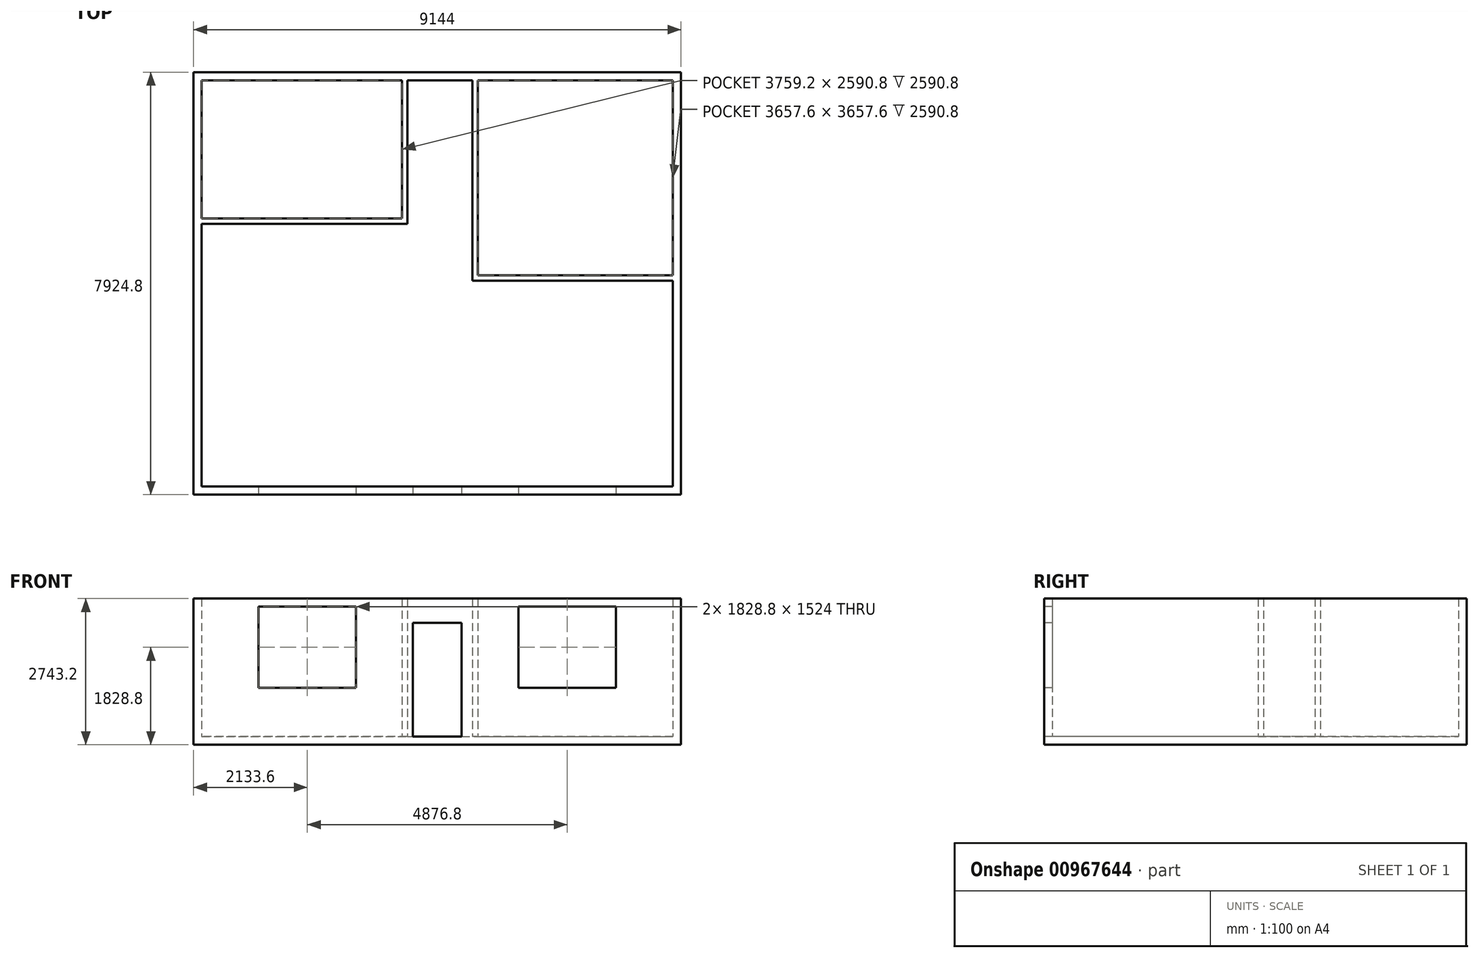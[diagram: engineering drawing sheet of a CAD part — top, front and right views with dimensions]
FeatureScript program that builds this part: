
annotation { "Feature Type Name" : "Feature", "Feature Type Description" : "" }
export const myFeature = defineFeature(function(context is Context, id is Id, definition is map)
    precondition{}
    {
        {
            var Q0;
            Q0=qCreatedBy(makeId("Top.planeOp"),FACE);
            var sketch = newSketch(context, id + "F0", { "sketchPlane" : qUnion([Q0])});
            skLineSegment(sketch, "E0.bottom", {"start": v(-4572, 3962.4) * mm, "end": v(4572, 3962.4) * mm});
            skLineSegment(sketch, "E0.top", {"start": v(-4572, -3962.4) * mm, "end": v(4572, -3962.4) * mm});
            skLineSegment(sketch, "E0.left", {"start": v(-4572, 3962.4) * mm, "end": v(-4572, -3962.4) * mm});
            skLineSegment(sketch, "E0.right", {"start": v(4572, 3962.4) * mm, "end": v(4572, -3962.4) * mm});
            skPoint(sketch, "E0.middle", {"position": v(0, 0) * mm});
            skSolve(sketch);
        }
        {
            var Q0;
            Q0=makeQuery(id+"F0.imprint","IMPRINT",FACE,{"disambiguationData":[TD([[makeQuery(id+"F0.imprint","IMPRINT",EDGE,{"derivedFrom":sQuery(id+"F0.wireOp",EDGE,"E0.bottom")}),-1.0]])]});
            extrude(context, id + "F1", {"entities" : qUnion([Q0]), "flatOperationType" : FlatOperationType.REMOVE, "depth" : 2743.2 * mm, "offsetDistance" : 30.48 * mm, "domain" : OperationDomain.MODEL});
        }
        {
            var Q0;
            Q0=makeQuery(id+"F1.opExtrude","CAP_FACE",FACE,{"disambiguationData":[OSD([sQuery(id+"F0.wireOp",EDGE,"E0.bottom"),sQuery(id+"F0.wireOp",EDGE,"E0.top"),sQuery(id+"F0.wireOp",EDGE,"E0.left"),sQuery(id+"F0.wireOp",EDGE,"E0.right")])],"isStart":false});
            shell(context, id + "F2", {"entities" : qUnion([Q0]), "thickness" : 152.4 * mm});
        }
        {
            var Q0;
            Q0=makeQuery(id+"F1.opExtrude","SWEPT_FACE",FACE,{"disambiguationData":[OSD([sQuery(id+"F0.wireOp",EDGE,"E0.top")])]});
            var sketch = newSketch(context, id + "F3", { "sketchPlane" : qUnion([Q0])});
            skLineSegment(sketch, "E1.bottom", {"start": v(457.2, 2286) * mm, "end": v(-457.2, 2286) * mm});
            skLineSegment(sketch, "E1.top", {"start": v(457.2, 152.4) * mm, "end": v(-457.2, 152.4) * mm});
            skLineSegment(sketch, "E1.left", {"start": v(457.2, 2286) * mm, "end": v(457.2, 152.4) * mm});
            skLineSegment(sketch, "E1.right", {"start": v(-457.2, 2286) * mm, "end": v(-457.2, 152.4) * mm});
            skPoint(sketch, "E1.middle", {"position": v(0, 1219.2) * mm});
            skLineSegment(sketch, "E2.bottom", {"start": v(-3352.8, 3657.6) * mm, "end": v(-914.4, 3657.6) * mm});
            skLineSegment(sketch, "E2.top", {"start": v(-3352.8, 6096) * mm, "end": v(-914.4, 6096) * mm});
            skLineSegment(sketch, "E2.left", {"start": v(-3352.8, 3657.6) * mm, "end": v(-3352.8, 6096) * mm});
            skLineSegment(sketch, "E2.right", {"start": v(-914.4, 3657.6) * mm, "end": v(-914.4, 6096) * mm});
            skPoint(sketch, "E2.middle", {"position": v(-2133.6, 4876.8) * mm});
            skLineSegment(sketch, "E3.bottom", {"start": v(914.4, 3657.6) * mm, "end": v(3352.8, 3657.6) * mm});
            skLineSegment(sketch, "E3.top", {"start": v(914.4, 6096) * mm, "end": v(3352.8, 6096) * mm});
            skLineSegment(sketch, "E3.left", {"start": v(914.4, 3657.6) * mm, "end": v(914.4, 6096) * mm});
            skLineSegment(sketch, "E3.right", {"start": v(3352.8, 3657.6) * mm, "end": v(3352.8, 6096) * mm});
            skPoint(sketch, "E3.middle", {"position": v(2133.6, 4876.8) * mm});
            skLineSegment(sketch, "E4.bottom", {"start": v(-3352.8, 2590.8) * mm, "end": v(-1524, 2590.8) * mm});
            skLineSegment(sketch, "E4.top", {"start": v(-3352.8, 1066.8) * mm, "end": v(-1524, 1066.8) * mm});
            skLineSegment(sketch, "E4.left", {"start": v(-3352.8, 2590.8) * mm, "end": v(-3352.8, 1066.8) * mm});
            skLineSegment(sketch, "E4.right", {"start": v(-1524, 2590.8) * mm, "end": v(-1524, 1066.8) * mm});
            skPoint(sketch, "E4.middle", {"position": v(-2438.4, 1828.8) * mm});
            skLineSegment(sketch, "E5.bottom", {"start": v(1524, 2590.8) * mm, "end": v(3352.8, 2590.8) * mm});
            skLineSegment(sketch, "E5.top", {"start": v(1524, 1066.8) * mm, "end": v(3352.8, 1066.8) * mm});
            skLineSegment(sketch, "E5.left", {"start": v(1524, 2590.8) * mm, "end": v(1524, 1066.8) * mm});
            skLineSegment(sketch, "E5.right", {"start": v(3352.8, 2590.8) * mm, "end": v(3352.8, 1066.8) * mm});
            skPoint(sketch, "E5.middle", {"position": v(2438.4, 1828.8) * mm});
            skLineSegment(sketch, "E6", {"start": v(-3352.8, 1066.8) * mm, "end": v(-4572, 1066.8) * mm, "construction": true});
            skLineSegment(sketch, "E7", {"start": v(3352.8, 1066.8) * mm, "end": v(4572, 1066.8) * mm, "construction": true});
            skSolve(sketch);
        }
        {
            var Q0;
            Q0 = qSketchRegion(id + "F3", true);
            var Q1;
            Q1=makeQuery(id+"F2.opShell","OFFSET_FACE",FACE,{"disambiguationData":[OSD([sQuery(id+"F0.wireOp",EDGE,"E0.top")])]});
            extrude(context, id + "F4", {"entities" : qUnion([Q0]), "operationType" : NewBodyOperationType.REMOVE, "endBound" : BoundingType.UP_TO_SURFACE, "oppositeDirection" : true, "depth" : 30.48 * mm, "endBoundEntityFace" : qUnion([Q1]), "offsetDistance" : 30.48 * mm});
        }
        {
            var Q0;
            Q0=makeQuery(id+"F4.boolean.opBoolean","MERGE",FACE,{"derivedFrom":[makeQuery(id+"F2.opShell","OFFSET_FACE",FACE,{"disambiguationData":[OSD([sQuery(id+"F0.wireOp",EDGE,"E0.bottom"),sQuery(id+"F0.wireOp",EDGE,"E0.top"),sQuery(id+"F0.wireOp",EDGE,"E0.left"),sQuery(id+"F0.wireOp",EDGE,"E0.right")])]})],"fromTools":[makeQuery(id+"F4.opExtrude","SWEPT_FACE",FACE,{"disambiguationData":[OSD([sQuery(id+"F3.wireOp",EDGE,"E1.top")])]})]});
            var sketch = newSketch(context, id + "F5", { "sketchPlane" : qUnion([Q0])});
            skLineSegment(sketch, "E8", {"start": v(4419.6, 50.8) * mm, "end": v(660.4, 50.8) * mm});
            skLineSegment(sketch, "E9", {"start": v(660.4, 50.8) * mm, "end": v(660.4, 3810) * mm});
            skLineSegment(sketch, "E10", {"start": v(660.4, 3810) * mm, "end": v(762, 3810) * mm});
            skLineSegment(sketch, "E11", {"start": v(762, 3810) * mm, "end": v(762, 152.4) * mm});
            skLineSegment(sketch, "E12", {"start": v(762, 152.4) * mm, "end": v(4419.6, 152.4) * mm});
            skLineSegment(sketch, "E13", {"start": v(4419.6, 152.4) * mm, "end": v(4419.6, 50.8) * mm});
            skLineSegment(sketch, "E14", {"start": v(-558.8, 3810) * mm, "end": v(-558.8, 1117.6) * mm});
            skLineSegment(sketch, "E15", {"start": v(-558.8, 1117.6) * mm, "end": v(-4419.6, 1117.6) * mm});
            skLineSegment(sketch, "E16", {"start": v(-4419.6, 1117.6) * mm, "end": v(-4419.6, 1219.2) * mm});
            skLineSegment(sketch, "E17", {"start": v(-4419.6, 1219.2) * mm, "end": v(-660.4, 1219.2) * mm});
            skLineSegment(sketch, "E18", {"start": v(-660.4, 1219.2) * mm, "end": v(-660.4, 3810) * mm});
            skLineSegment(sketch, "E19", {"start": v(-660.4, 3810) * mm, "end": v(-558.8, 3810) * mm});
            skSolve(sketch);
        }
        {
            var Q0;
            Q0 = qSketchRegion(id + "F5", true);
            var Q1;
            Q1=makeQuery(id+"F1.opExtrude","CAP_FACE",FACE,{"disambiguationData":[OSD([sQuery(id+"F0.wireOp",EDGE,"E0.bottom"),sQuery(id+"F0.wireOp",EDGE,"E0.top"),sQuery(id+"F0.wireOp",EDGE,"E0.left"),sQuery(id+"F0.wireOp",EDGE,"E0.right")])],"isStart":false});
            extrude(context, id + "F6", {"entities" : qUnion([Q0]), "operationType" : NewBodyOperationType.ADD, "endBound" : BoundingType.UP_TO_SURFACE, "depth" : 30.48 * mm, "endBoundEntityFace" : qUnion([Q1]), "offsetDistance" : 30.48 * mm});
        }
    });
